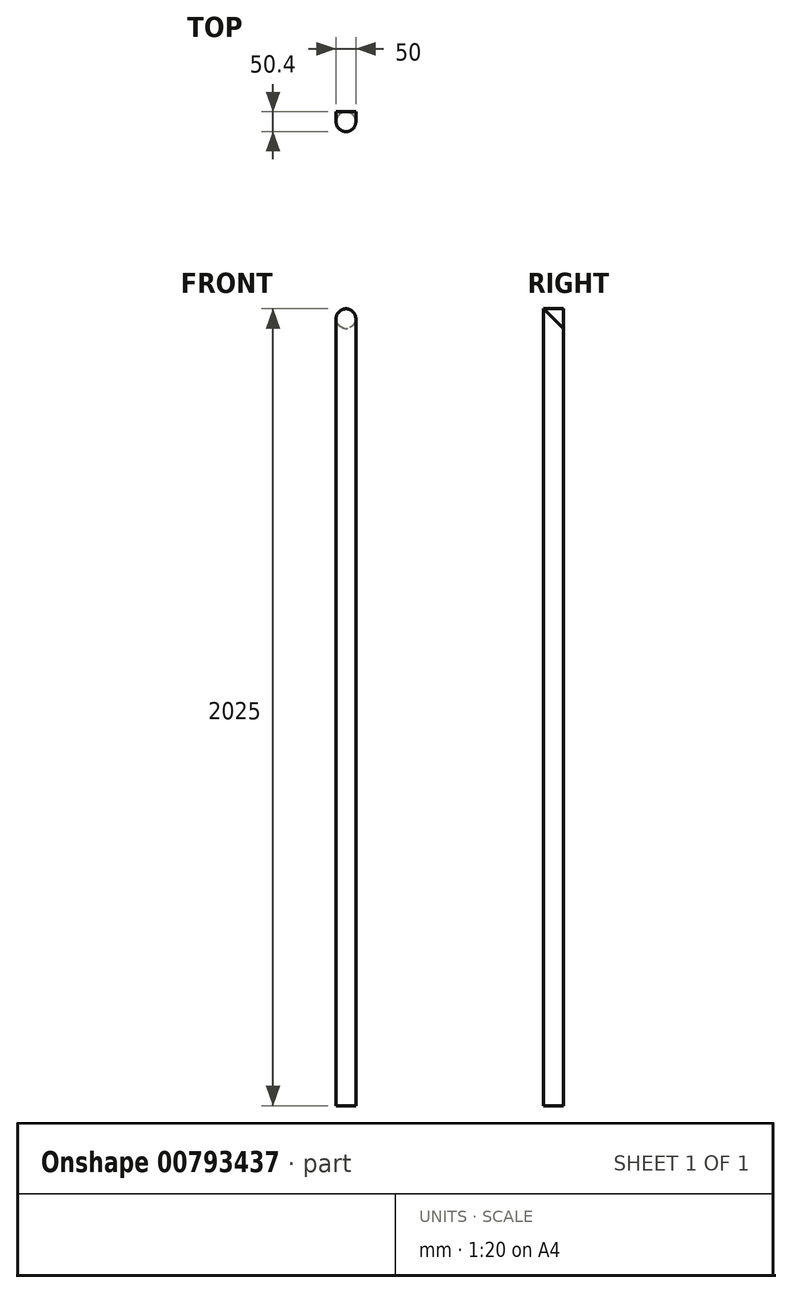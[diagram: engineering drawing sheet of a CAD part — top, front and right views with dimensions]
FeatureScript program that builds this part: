
annotation { "Feature Type Name" : "Feature", "Feature Type Description" : "" }
export const myFeature = defineFeature(function(context is Context, id is Id, definition is map)
    precondition{}
    {
        {
            var Q0;
            Q0=qCreatedBy(makeId("Right.planeOp"),FACE);
            var sketch = newSketch(context, id + "F0", { "sketchPlane" : qUnion([Q0])});
            skLineSegment(sketch, "E0", {"start": v(0, 0) * mm, "end": v(0, 2000) * mm});
            skLineSegment(sketch, "E1", {"start": v(0, 2000) * mm, "end": v(25.4, 2000) * mm});
            skSolve(sketch);
        }
        {
            var Q0;
            Q0=qCreatedBy(makeId("Top.planeOp"),FACE);
            var sketch = newSketch(context, id + "F1", { "sketchPlane" : qUnion([Q0])});
            skCircle(sketch, "E2", {"center": v(0, 0) * mm, "radius": 25 * mm});
            skSolve(sketch);
        }
        {
            var Q0;
            Q0=makeQuery(id+"F1.imprint","IMPRINT",FACE,{"disambiguationData":[TD([[makeQuery(id+"F1.imprint","IMPRINT",EDGE,{"derivedFrom":sQuery(id+"F1.wireOp",EDGE,"E2")}),1.0]])]});
            var Q1;
            Q1=sQuery(id+"F0.wireOp",EDGE,"E0");
            var Q2;
            Q2=sQuery(id+"F0.wireOp",EDGE,"E1");
            sweep(context, id + "F2", {"profiles" : qUnion([Q0]), "path" : qUnion([Q1, Q2])});
        }
    });
